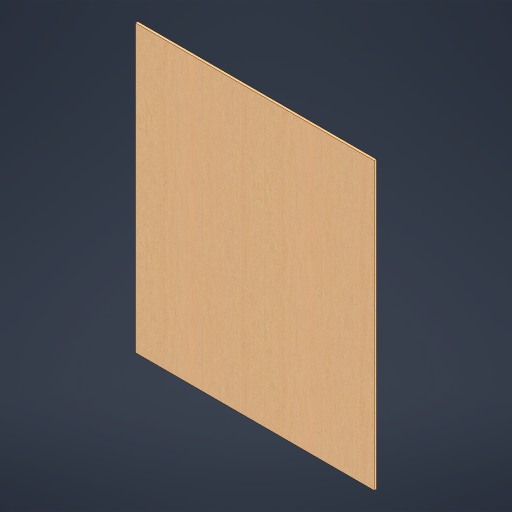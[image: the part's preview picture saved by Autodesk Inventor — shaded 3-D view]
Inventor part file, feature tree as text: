
AUTODESK INVENTOR PART (.ipt)
format: ipt  version: 2024 (Build 280153000, 153)  size: 311,808 bytes
history: native  units: mm
features: other x2, extrude x1, sketch x1
ambient origin geometry x8: Origin, YZ Plane, XZ Plane, XY Plane, X Axis, Y Axis, Z Axis, Center Point
bodies: Body1 (feature_tree)
feature tree (4):
  other  "솔리드1"
  extrude  "돌출1"  Depth=510.0mm
  sketch  "스케치1"
  other  "Finish1"
